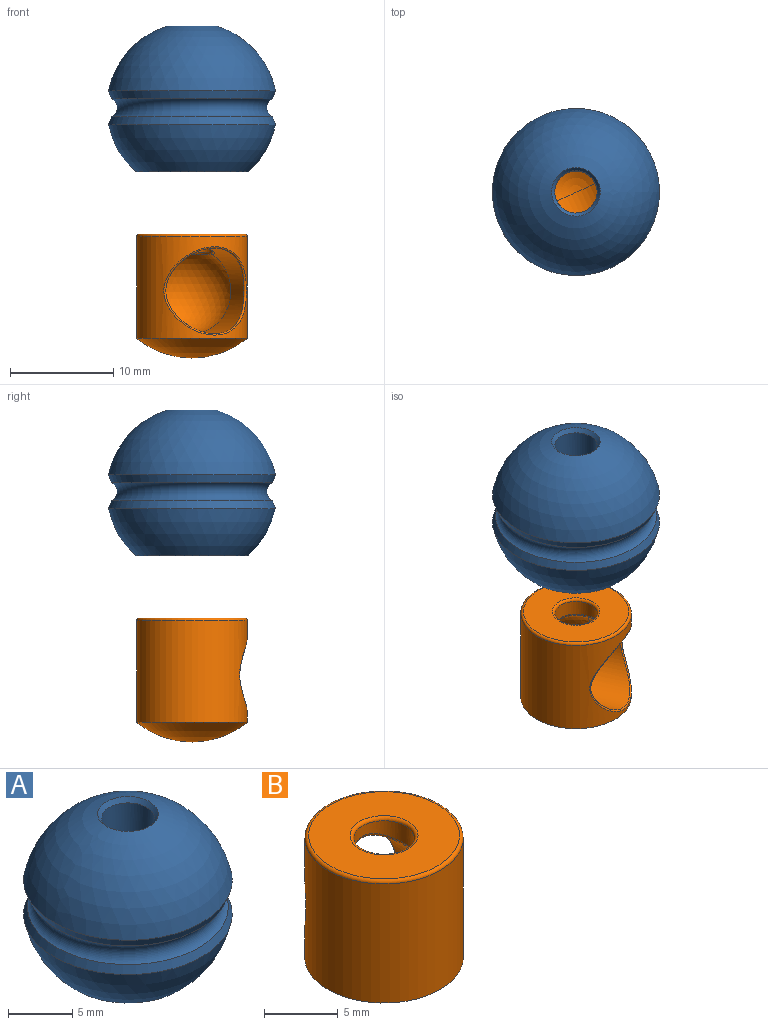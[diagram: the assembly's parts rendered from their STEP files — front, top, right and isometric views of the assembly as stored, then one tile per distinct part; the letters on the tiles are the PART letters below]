
ASSEMBLY  parts=2 mates=1
PART A: 16 faces, bbox 17.9x17.9x14.1 mm
  f0: cylinder r=2.05mm len=4.1mm, axis (0,0,-1), area 45.2mm2, adj f1,f14
  f1: cone r=2.35mm half-angle=36.9deg, axis (0,0,1), area 6.9mm2, adj f0,f2
  f2: sphere r=8.25mm, area 325.4mm2, adj f1,f3
  f3: cone r=7.79mm half-angle=21.9deg, axis (0,0,1), area 39.9mm2, adj f2,f4
  f4: torus R=8.25mm, axis (0,0,-1), area 102.1mm2, adj f3,f5
  f5: cone r=7.79mm half-angle=21.9deg, axis (0,0,-1), area 39.9mm2, adj f4,f6
  f6: sphere r=8.25mm, area 236.6mm2, adj f5,f7
  f7: cylinder r=5.45mm len=10.9mm, axis (0,0,-1), area 62.5mm2, adj f6,f8
  f8: torus R=6.45mm, axis (0,0,-1), area 11.7mm2, adj f7,f9
  f9: revolved ~12.3x12.3mm, area 352mm2, adj f8,f10
  f10: torus R=3.74mm, axis (0,0,-1), area 38.3mm2, adj f9,f11
  f11: torus R=3.45mm, axis (0,0,-1), area 7mm2, adj f10,f12
  f12: cylinder r=3.15mm len=6.3mm, axis (0,0,-1), area 29.9mm2, adj f11,f15
  f13: plane 5.8x5.8mm, normal (0,0,-1), area 9.8mm2, adj f14,f15
  f14: torus R=2.3mm, axis (0,0,1), area 5.3mm2, adj f0,f13
  f15: torus R=2.9mm, axis (0,0,1), area 7.5mm2, adj f12,f13
PART B: 11 faces, bbox 11.6x11.6x12 mm
  f0: sphere r=8.5mm, area 101.2mm2, adj f3
  f1: sphere r=4.15mm, area 100.2mm2, adj f4,f7
  f2: cylinder r=2.05mm len=4.1mm, axis (0,0,-1), area 17.3mm2, adj f7,f8,f9
  f3: cylinder r=5.35mm len=10.7mm, axis (0,0,-1), area 265.6mm2, adj f0,f5,f10
  f4: cylinder r=4.15mm len=8.3mm, axis (0,-1,0), area 101.1mm2, adj f1,f5,f8
  f5: bspline ~8.76x8.56mm, area 7.1mm2, adj f3,f4
  f6: plane 10.2x10.2mm, normal (0,0,1), area 65.1mm2, adj f9,f10
  f7: torus R=2.3mm, axis (0,0,-1), area 1.7mm2, adj f1,f2,f8
  f8: bspline ~4.34x2.76mm, area 2.2mm2, adj f2,f4,f7
  f9: torus R=2.3mm, axis (0,0,-1), area 5.3mm2, adj f2,f6
  f10: torus R=5.1mm, axis (0,0,-1), area 13mm2, adj f3,f6
PLACE A rot(axis=(0,0,-1),180deg) t=(0,0,-4)mm
PLACE B rot(axis=(0,0,-1),155.6deg) t=(0,0,-19.72)mm
MATE cylindrical A.f0 <-> B.f2  axis (0,0,-1) through (0,0,-0.25)mm
